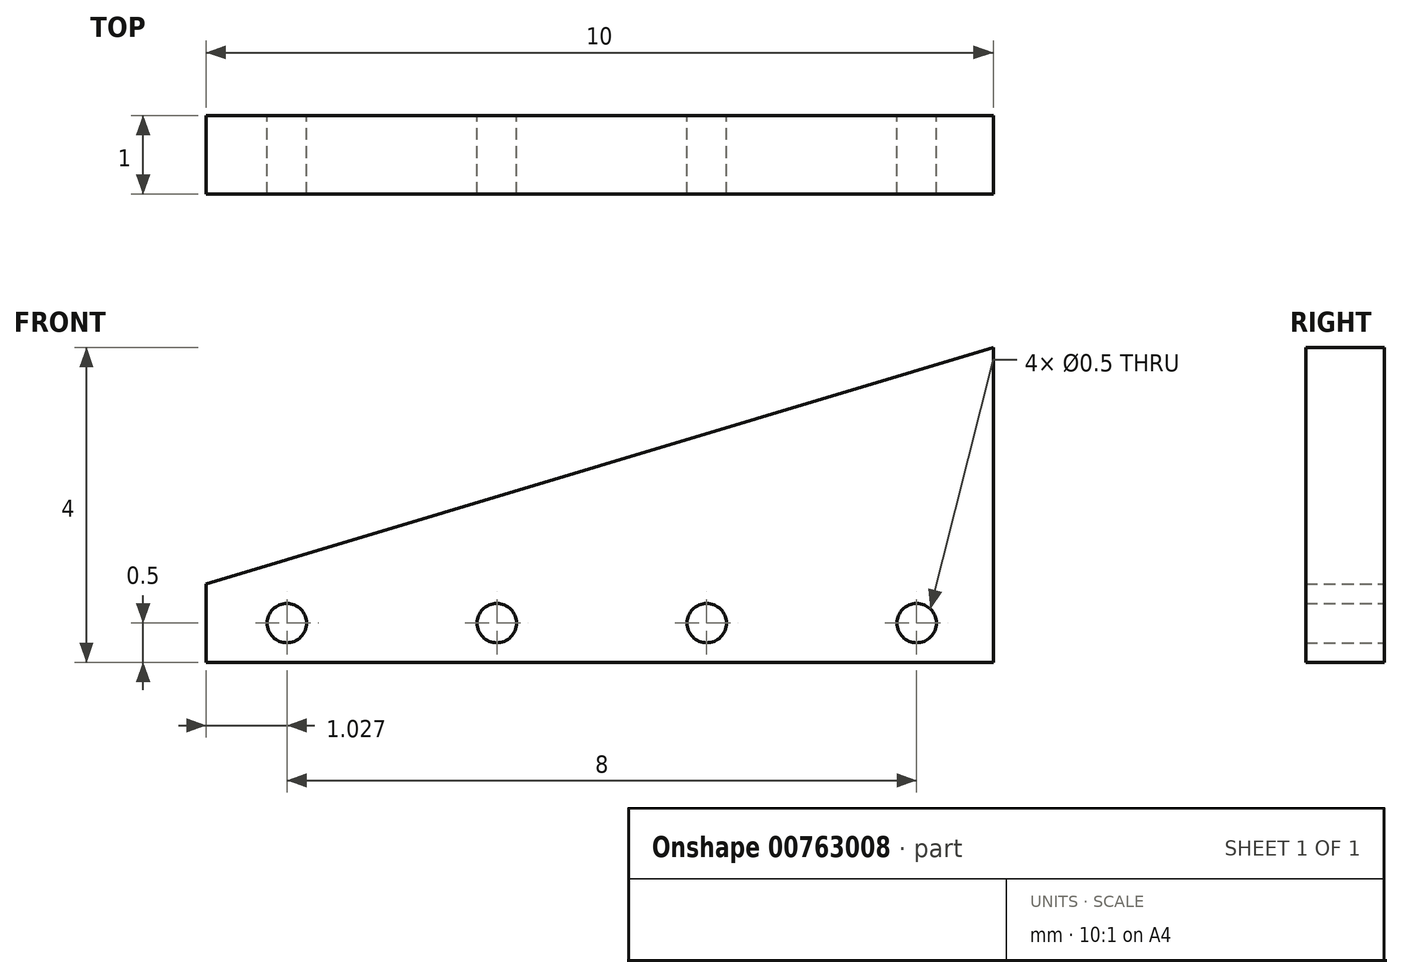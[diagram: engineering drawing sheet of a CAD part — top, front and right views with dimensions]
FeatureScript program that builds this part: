
annotation { "Feature Type Name" : "Feature", "Feature Type Description" : "" }
export const myFeature = defineFeature(function(context is Context, id is Id, definition is map)
    precondition{}
    {
        {
            var Q0;
            Q0=qCreatedBy(makeId("Front.planeOp"),FACE);
            var sketch = newSketch(context, id + "F0", { "sketchPlane" : qUnion([Q0])});
            skLineSegment(sketch, "E0", {"start": v(0, 0) * mm, "end": v(0, 4) * mm});
            skLineSegment(sketch, "E1", {"start": v(0, 4) * mm, "end": v(-10, 1) * mm});
            skLineSegment(sketch, "E2", {"start": v(-10, 1) * mm, "end": v(-10, 0) * mm});
            skLineSegment(sketch, "E3", {"start": v(-10, 0) * mm, "end": v(0, 0) * mm});
            skCircle(sketch, "E4", {"center": v(-8.97, 0.5) * mm, "radius": 0.25 * mm});
            skCircle(sketch, "E5", {"center": v(-6.3, 0.5) * mm, "radius": 0.25 * mm});
            skCircle(sketch, "E6", {"center": v(-3.64, 0.5) * mm, "radius": 0.25 * mm});
            skCircle(sketch, "E7", {"center": v(-0.97, 0.5) * mm, "radius": 0.25 * mm});
            skPoint(sketch, "E8.orphan", {"position": v(-10, 0.5) * mm});
            skSolve(sketch);
        }
        {
            var Q0;
            Q0=makeQuery(id+"F0.imprint","IMPRINT",FACE,{"disambiguationData":[TD([[makeQuery(id+"F0.imprint","IMPRINT",EDGE,{"derivedFrom":sQuery(id+"F0.wireOp",EDGE,"E0")}),1.0]])]});
            extrude(context, id + "F1", {"entities" : qUnion([Q0]), "depth" : 1 * mm, "offsetDistance" : 25.4 * mm});
        }
    });
